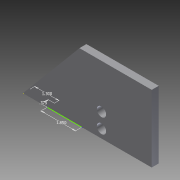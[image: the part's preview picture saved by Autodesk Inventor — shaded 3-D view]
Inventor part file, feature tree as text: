
AUTODESK INVENTOR PART (.ipt)
format: ipt  version: 2012 (Build 160160000, 160)  size: 158,720 bytes
history: native  units: in
note: dims shown in document units (in); Inventor stores cm internally (conversion verified against a paired STEP export)
features: other x3, sketch x1
ambient origin geometry x8: Origin, YZ Plane, XZ Plane, XY Plane, X Axis, Y Axis, Z Axis, Center Point
bodies: Solid1 (feature_tree)
feature tree (4):
  other  "Chassis Right3.ipt"
  other  "Solid1::Chassis Right3.ipt"
  sketch  "Sketch1"  dims[d0=0.3937in]
  other  "TaggingFeature1"
